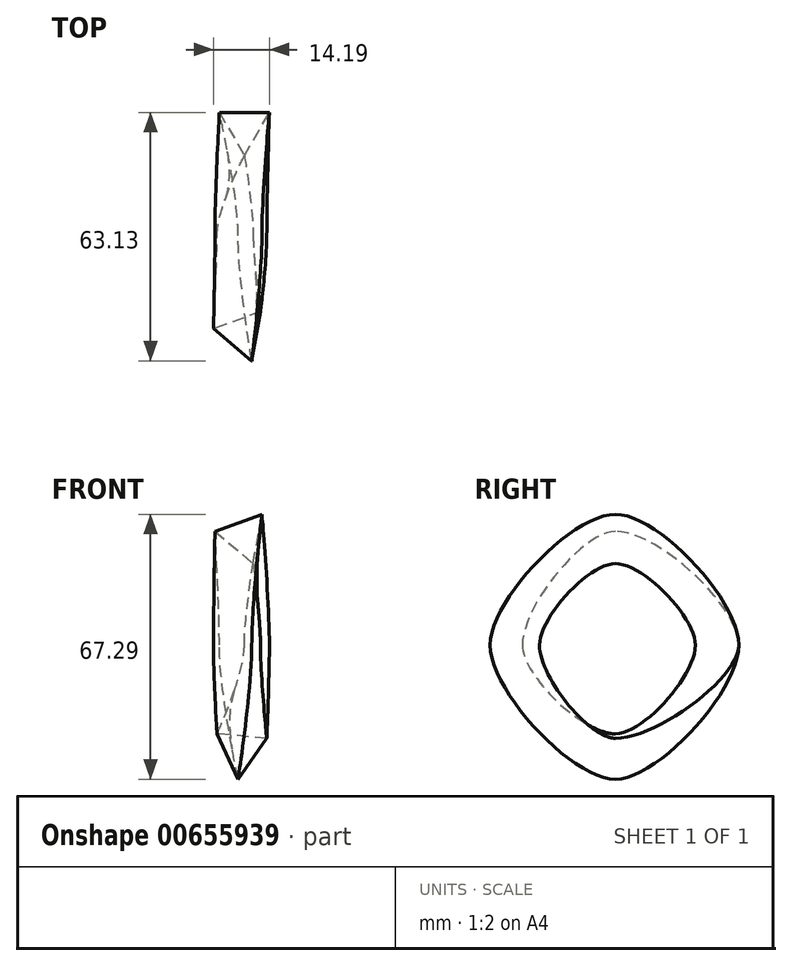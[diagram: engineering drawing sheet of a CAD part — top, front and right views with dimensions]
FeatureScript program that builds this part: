
annotation { "Feature Type Name" : "Feature", "Feature Type Description" : "" }
export const myFeature = defineFeature(function(context is Context, id is Id, definition is map)
    precondition{}
    {
        {
            var Q0;
            Q0=qCreatedBy(makeId("Top.planeOp"),FACE);
            var sketch = newSketch(context, id + "F0", { "sketchPlane" : qUnion([Q0])});
            skLineSegment(sketch, "E0", {"start": v(-6.35, 31.32) * mm, "end": v(6.35, 31.32) * mm});
            skLineSegment(sketch, "E1", {"start": v(-6.35, 31.32) * mm, "end": v(0, 20.32) * mm});
            skLineSegment(sketch, "E2", {"start": v(0, 20.32) * mm, "end": v(6.35, 31.32) * mm});
            skLineSegment(sketch, "E3", {"start": v(1.89, -31.81) * mm, "end": v(-7.84, -23.65) * mm});
            skLineSegment(sketch, "E4", {"start": v(1.89, -31.81) * mm, "end": v(4.1, -19.3) * mm});
            skLineSegment(sketch, "E5", {"start": v(4.1, -19.3) * mm, "end": v(-7.84, -23.65) * mm});
            skSolve(sketch);
        }
        {
            var Q0;
            Q0=qCreatedBy(makeId("Front.planeOp"),FACE);
            var sketch = newSketch(context, id + "F1", { "sketchPlane" : qUnion([Q0])});
            skLineSegment(sketch, "E6", {"start": v(-1.59, -34.07) * mm, "end": v(-6.95, -22.56) * mm});
            skLineSegment(sketch, "E7", {"start": v(-1.59, -34.07) * mm, "end": v(5.7, -23.66) * mm});
            skLineSegment(sketch, "E8", {"start": v(5.7, -23.66) * mm, "end": v(-6.95, -22.56) * mm});
            skLineSegment(sketch, "E9", {"start": v(-7.48, 28.88) * mm, "end": v(4.46, 33.22) * mm});
            skLineSegment(sketch, "E10", {"start": v(-7.48, 28.88) * mm, "end": v(2.25, 20.72) * mm});
            skLineSegment(sketch, "E11", {"start": v(2.25, 20.72) * mm, "end": v(4.46, 33.22) * mm});
            skSolve(sketch);
        }
        {
            var Q0;
            Q0=makeQuery(id+"F1.imprint","IMPRINT",FACE,{"disambiguationData":[TD([[makeQuery(id+"F1.imprint","IMPRINT",EDGE,{"derivedFrom":sQuery(id+"F1.wireOp",EDGE,"E9")}),-1.0]])]});
            var Q1;
            Q1=makeQuery(id+"F0.imprint","IMPRINT",FACE,{"disambiguationData":[TD([[makeQuery(id+"F0.imprint","IMPRINT",EDGE,{"derivedFrom":sQuery(id+"F0.wireOp",EDGE,"E3")}),-1.0]])]});
            loft(context, id + "F2", {"startCondition" : LoftEndDerivativeType.NORMAL_TO_PROFILE, "startMagnitude" : 1, "endCondition" : LoftEndDerivativeType.NORMAL_TO_PROFILE, "endMagnitude" : 1, "sheetProfilesArray" : [{ "sheetProfileEntities" : qUnion([Q0]) }, { "sheetProfileEntities" : qUnion([Q1]) }]});
        }
        {
            var Q1;
            Q1=makeQuery(id+"F0.imprint","IMPRINT",FACE,{"disambiguationData":[TD([[makeQuery(id+"F0.imprint","IMPRINT",EDGE,{"derivedFrom":sQuery(id+"F0.wireOp",EDGE,"E3")}),-1.0]])]});
            var Q2;
            Q2=makeQuery(id+"F1.imprint","IMPRINT",FACE,{"disambiguationData":[TD([[makeQuery(id+"F1.imprint","IMPRINT",EDGE,{"derivedFrom":sQuery(id+"F1.wireOp",EDGE,"E6")}),-1.0]])]});
            loft(context, id + "F3", {"operationType" : NewBodyOperationType.ADD, "startCondition" : LoftEndDerivativeType.NORMAL_TO_PROFILE, "startMagnitude" : 1, "endCondition" : LoftEndDerivativeType.NORMAL_TO_PROFILE, "endMagnitude" : 1, "sheetProfilesArray" : [{ "sheetProfileEntities" : qUnion([Q1]) }, { "sheetProfileEntities" : qUnion([Q2]) }]});
        }
        {
            var Q1;
            Q1=makeQuery(id+"F1.imprint","IMPRINT",FACE,{"disambiguationData":[TD([[makeQuery(id+"F1.imprint","IMPRINT",EDGE,{"derivedFrom":sQuery(id+"F1.wireOp",EDGE,"E6")}),-1.0]])]});
            var Q2;
            Q2=makeQuery(id+"F0.imprint","IMPRINT",FACE,{"disambiguationData":[TD([[makeQuery(id+"F0.imprint","IMPRINT",EDGE,{"derivedFrom":sQuery(id+"F0.wireOp",EDGE,"E0")}),-1.0]])]});
            loft(context, id + "F4", {"operationType" : NewBodyOperationType.ADD, "startCondition" : LoftEndDerivativeType.NORMAL_TO_PROFILE, "startMagnitude" : 1, "endCondition" : LoftEndDerivativeType.NORMAL_TO_PROFILE, "endMagnitude" : 1, "sheetProfilesArray" : [{ "sheetProfileEntities" : qUnion([Q1]) }, { "sheetProfileEntities" : qUnion([Q2]) }]});
        }
        {
            var Q1;
            Q1=makeQuery(id+"F0.imprint","IMPRINT",FACE,{"disambiguationData":[TD([[makeQuery(id+"F0.imprint","IMPRINT",EDGE,{"derivedFrom":sQuery(id+"F0.wireOp",EDGE,"E0")}),-1.0]])]});
            var Q2;
            Q2=makeQuery(id+"F1.imprint","IMPRINT",FACE,{"disambiguationData":[TD([[makeQuery(id+"F1.imprint","IMPRINT",EDGE,{"derivedFrom":sQuery(id+"F1.wireOp",EDGE,"E9")}),-1.0]])]});
            loft(context, id + "F5", {"operationType" : NewBodyOperationType.ADD, "startCondition" : LoftEndDerivativeType.NORMAL_TO_PROFILE, "startMagnitude" : 1, "endCondition" : LoftEndDerivativeType.NORMAL_TO_PROFILE, "endMagnitude" : 1, "sheetProfilesArray" : [{ "sheetProfileEntities" : qUnion([Q1]) }, { "sheetProfileEntities" : qUnion([Q2]) }]});
        }
    });
